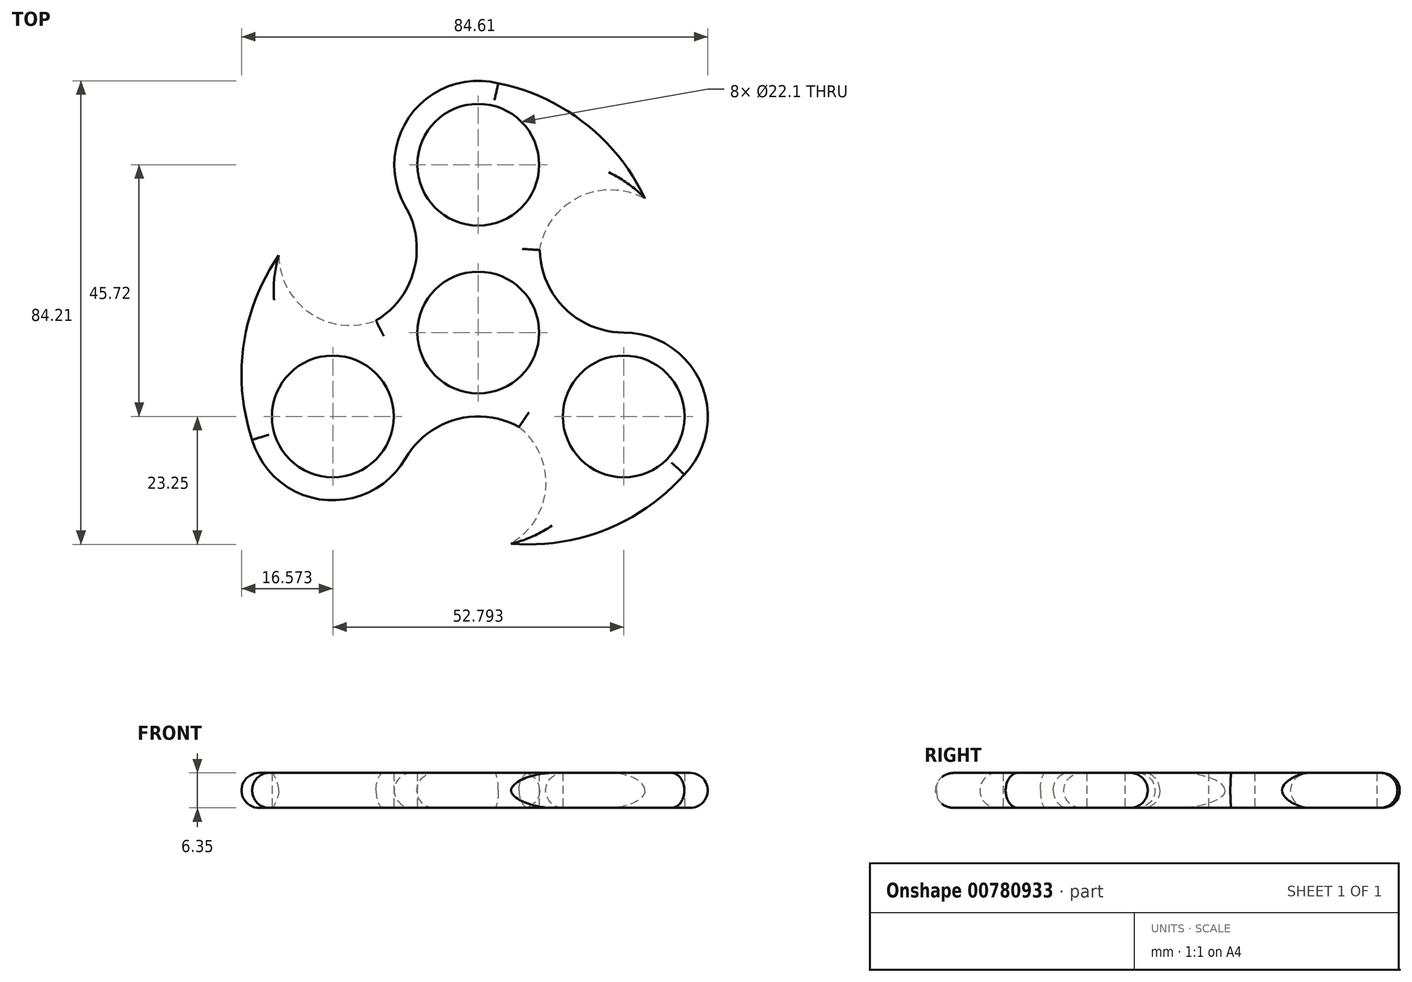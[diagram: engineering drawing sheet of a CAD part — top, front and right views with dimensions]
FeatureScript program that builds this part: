
annotation { "Feature Type Name" : "Feature", "Feature Type Description" : "" }
export const myFeature = defineFeature(function(context is Context, id is Id, definition is map)
    precondition{}
    {
        {
            var Q0;
            Q0=qCreatedBy(makeId("Top.planeOp"),FACE);
            var sketch = newSketch(context, id + "F0", { "sketchPlane" : qUnion([Q0])});
            skCircle(sketch, "E0", {"center": v(0, 0) * mm, "radius": 11.05 * mm});
            skCircle(sketch, "E1", {"center": v(0, 30.48) * mm, "radius": 11.05 * mm});
            skArc(sketch, "E2", {"start": v(3.63, 45.28) * mm, "mid": v(-12.19, 39.63) * mm, "end": v(-13.2, 22.86) * mm});
            skCircle(sketch, "E3.1.0", {"center": v(-26.4, -15.24) * mm, "radius": 11.05 * mm});
            skArc(sketch, "E3.1.1", {"start": v(-41.03, -19.5) * mm, "mid": v(-28.23, -30.37) * mm, "end": v(-13.2, -22.86) * mm});
            skCircle(sketch, "E3.2.0", {"center": v(26.4, -15.24) * mm, "radius": 11.05 * mm});
            skArc(sketch, "E3.2.1", {"start": v(37.4, -25.79) * mm, "mid": v(40.41, -9.26) * mm, "end": v(26.4, 0) * mm});
            skArc(sketch, "E4", {"start": v(-18.55, 2.17) * mm, "mid": v(-11.64, 11.42) * mm, "end": v(-13.2, 22.86) * mm});
            skArc(sketch, "E5.1.0", {"start": v(7.4, -17.15) * mm, "mid": v(-4.07, -15.8) * mm, "end": v(-13.2, -22.86) * mm});
            skArc(sketch, "E5.2.0", {"start": v(11.16, 14.98) * mm, "mid": v(15.71, 4.37) * mm, "end": v(26.4, 0) * mm});
            skArc(sketch, "E6", {"start": v(30.24, 24.34) * mm, "mid": v(18.26, 24.64) * mm, "end": v(11.16, 14.98) * mm});
            skArc(sketch, "E7.1.1", {"start": v(-36.2, 14.01) * mm, "mid": v(-30.46, 3.5) * mm, "end": v(-18.55, 2.17) * mm});
            skArc(sketch, "E7.2.1", {"start": v(5.96, -38.36) * mm, "mid": v(12.2, -28.13) * mm, "end": v(7.4, -17.15) * mm});
            skPoint(sketch, "E8.orphan", {"position": v(13.2, 22.86) * mm});
            skPoint(sketch, "E9.orphan", {"position": v(13.2, -22.86) * mm});
            skPoint(sketch, "E10.orphan", {"position": v(-26.4, 0) * mm});
            skArc(sketch, "E11", {"start": v(-36.2, 14.01) * mm, "mid": v(-42.58, -2.17) * mm, "end": v(-41.03, -19.5) * mm});
            skArc(sketch, "E12.1.0", {"start": v(5.96, -38.36) * mm, "mid": v(23.17, -35.8) * mm, "end": v(37.4, -25.79) * mm});
            skArc(sketch, "E12.2.0", {"start": v(30.24, 24.34) * mm, "mid": v(19.41, 37.96) * mm, "end": v(3.63, 45.28) * mm});
            skPoint(sketch, "E7.1.0.end.orphan", {"position": v(-41.03, -10.99) * mm});
            skSolve(sketch);
        }
        {
            var Q0;
            Q0=qSketchRegion(id+"F0",true);
            extrude(context, id + "F1", {"entities" : qUnion([Q0]), "depth" : 6.35 * mm, "offsetDistance" : 25.4 * mm});
        }
        {
            var Q0;
            Q0=makeQuery(id+"F1.opExtrude","CAP_EDGE",EDGE,{"disambiguationData":[OSD([sQuery(id+"F0.wireOp",EDGE,"E7.1.0")])],"isStart":false});
            var Q1;
            Q1=makeQuery(id+"F1.opExtrude","CAP_EDGE",EDGE,{"disambiguationData":[OSD([sQuery(id+"F0.wireOp",EDGE,"E7.1.1")])],"isStart":false});
            var Q2;
            Q2=makeQuery(id+"F1.opExtrude","CAP_EDGE",EDGE,{"disambiguationData":[OSD([sQuery(id+"F0.wireOp",EDGE,"E4")])],"isStart":false});
            var Q3;
            Q3=makeQuery(id+"F1.opExtrude","CAP_EDGE",EDGE,{"disambiguationData":[OSD([sQuery(id+"F0.wireOp",EDGE,"E2")])],"isStart":false});
            var Q4;
            Q4=makeQuery(id+"F1.opExtrude","CAP_EDGE",EDGE,{"disambiguationData":[OSD([sQuery(id+"F0.wireOp",EDGE,"lhcFQ0OA-2SQs-v3oS-6c17-3j6k09Nsckje")])],"isStart":false});
            var Q5;
            Q5=makeQuery(id+"F1.opExtrude","CAP_EDGE",EDGE,{"disambiguationData":[OSD([sQuery(id+"F0.wireOp",EDGE,"E6")])],"isStart":false});
            var Q6;
            Q6=makeQuery(id+"F1.opExtrude","CAP_EDGE",EDGE,{"disambiguationData":[OSD([sQuery(id+"F0.wireOp",EDGE,"E5.2.0")])],"isStart":false});
            var Q7;
            Q7=makeQuery(id+"F1.opExtrude","CAP_EDGE",EDGE,{"disambiguationData":[OSD([sQuery(id+"F0.wireOp",EDGE,"E3.2.1")])],"isStart":false});
            var Q8;
            Q8=makeQuery(id+"F1.opExtrude","CAP_EDGE",EDGE,{"disambiguationData":[OSD([sQuery(id+"F0.wireOp",EDGE,"E7.2.0")])],"isStart":false});
            var Q9;
            Q9=makeQuery(id+"F1.opExtrude","CAP_EDGE",EDGE,{"disambiguationData":[OSD([sQuery(id+"F0.wireOp",EDGE,"E7.2.1")])],"isStart":false});
            var Q10;
            Q10=makeQuery(id+"F1.opExtrude","CAP_EDGE",EDGE,{"disambiguationData":[OSD([sQuery(id+"F0.wireOp",EDGE,"E5.1.0")])],"isStart":false});
            var Q11;
            Q11=makeQuery(id+"F1.opExtrude","CAP_EDGE",EDGE,{"disambiguationData":[OSD([sQuery(id+"F0.wireOp",EDGE,"E3.1.1")])],"isStart":false});
            var Q12;
            Q12=makeQuery(id+"F1.opExtrude","CAP_EDGE",EDGE,{"disambiguationData":[OSD([sQuery(id+"F0.wireOp",EDGE,"E7.1.0")])],"isStart":true});
            var Q13;
            Q13=makeQuery(id+"F1.opExtrude","CAP_EDGE",EDGE,{"disambiguationData":[OSD([sQuery(id+"F0.wireOp",EDGE,"E3.1.1")])],"isStart":true});
            var Q14;
            Q14=makeQuery(id+"F1.opExtrude","CAP_EDGE",EDGE,{"disambiguationData":[OSD([sQuery(id+"F0.wireOp",EDGE,"E5.1.0")])],"isStart":true});
            var Q15;
            Q15=makeQuery(id+"F1.opExtrude","CAP_EDGE",EDGE,{"disambiguationData":[OSD([sQuery(id+"F0.wireOp",EDGE,"E7.2.1")])],"isStart":true});
            var Q16;
            Q16=makeQuery(id+"F1.opExtrude","CAP_EDGE",EDGE,{"disambiguationData":[OSD([sQuery(id+"F0.wireOp",EDGE,"E7.2.0")])],"isStart":true});
            var Q17;
            Q17=makeQuery(id+"F1.opExtrude","CAP_EDGE",EDGE,{"disambiguationData":[OSD([sQuery(id+"F0.wireOp",EDGE,"E5.2.0")])],"isStart":true});
            var Q18;
            Q18=makeQuery(id+"F1.opExtrude","CAP_EDGE",EDGE,{"disambiguationData":[OSD([sQuery(id+"F0.wireOp",EDGE,"E3.2.1")])],"isStart":true});
            var Q19;
            Q19=makeQuery(id+"F1.opExtrude","CAP_EDGE",EDGE,{"disambiguationData":[OSD([sQuery(id+"F0.wireOp",EDGE,"E6")])],"isStart":true});
            var Q20;
            Q20=makeQuery(id+"F1.opExtrude","CAP_EDGE",EDGE,{"disambiguationData":[OSD([sQuery(id+"F0.wireOp",EDGE,"lhcFQ0OA-2SQs-v3oS-6c17-3j6k09Nsckje")])],"isStart":true});
            var Q21;
            Q21=makeQuery(id+"F1.opExtrude","CAP_EDGE",EDGE,{"disambiguationData":[OSD([sQuery(id+"F0.wireOp",EDGE,"E2")])],"isStart":true});
            var Q22;
            Q22=makeQuery(id+"F1.opExtrude","CAP_EDGE",EDGE,{"disambiguationData":[OSD([sQuery(id+"F0.wireOp",EDGE,"E4")])],"isStart":true});
            var Q23;
            Q23=makeQuery(id+"F1.opExtrude","CAP_EDGE",EDGE,{"disambiguationData":[OSD([sQuery(id+"F0.wireOp",EDGE,"E7.1.1")])],"isStart":true});
            fillet(context, id + "F2", {"entities" : qUnion([Q0, Q1, Q2, Q3, Q4, Q5, Q6, Q7, Q8, Q9, Q10, Q11, Q12, Q13, Q14, Q15, Q16, Q17, Q18, Q19, Q20, Q21, Q22, Q23]), "radius" : 3.17 * mm, "tangentPropagation" : true, "allowEdgeOverflow" : false});
        }
    });
